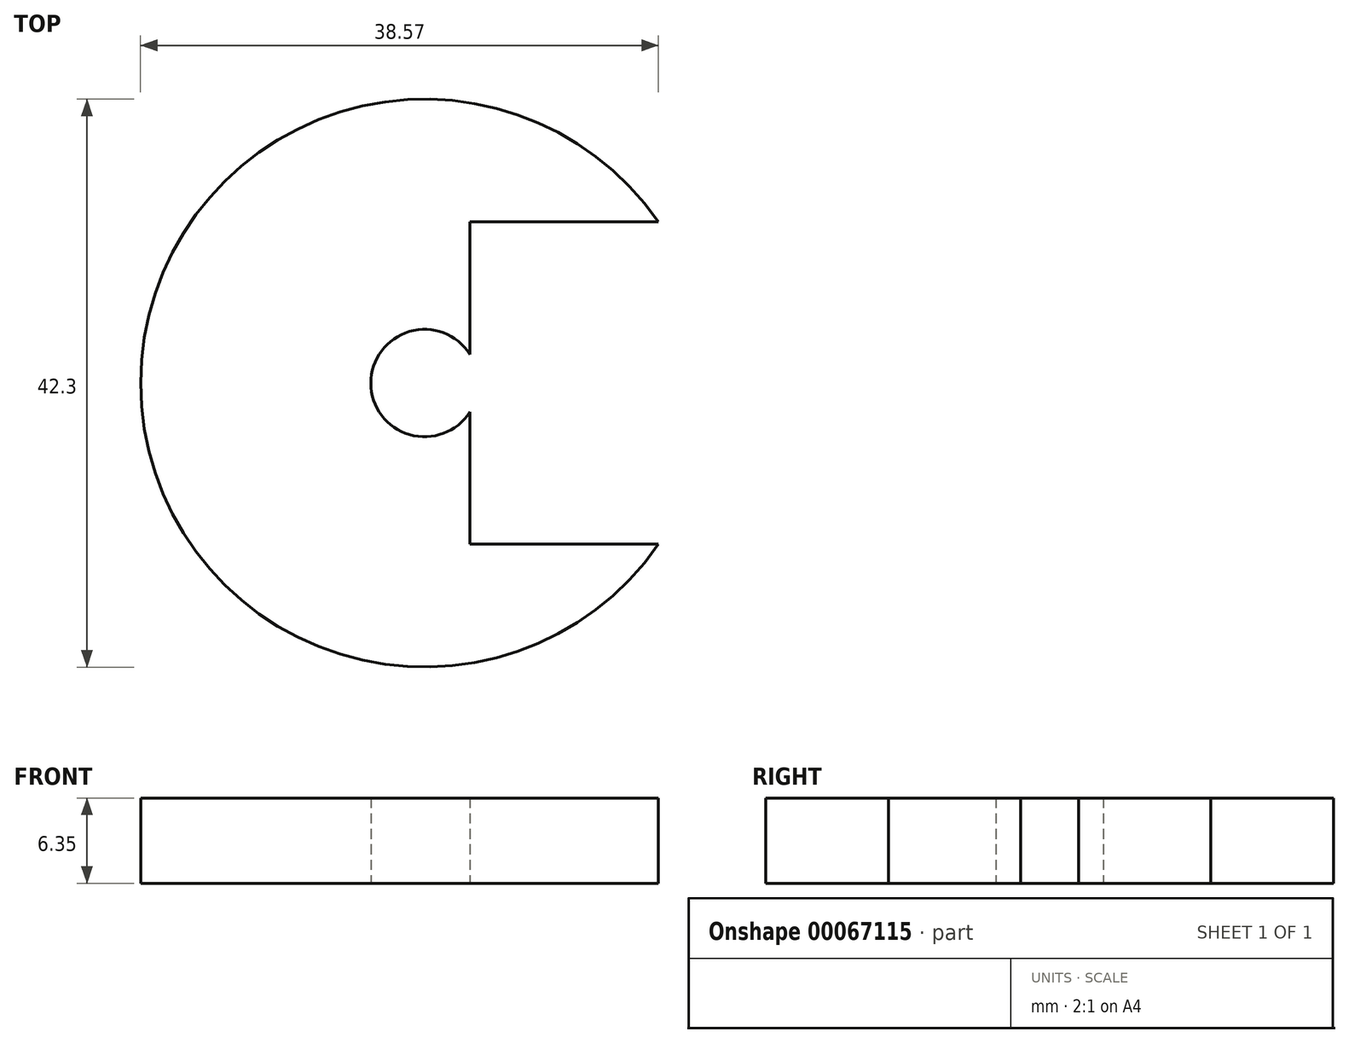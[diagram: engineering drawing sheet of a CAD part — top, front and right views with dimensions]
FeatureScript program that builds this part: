
annotation { "Feature Type Name" : "Feature", "Feature Type Description" : "" }
export const myFeature = defineFeature(function(context is Context, id is Id, definition is map)
    precondition{}
    {
        {
            var Q0;
            Q0=qCreatedBy(makeId("Top.planeOp"),FACE);
            var sketch = newSketch(context, id + "F0", { "sketchPlane" : qUnion([Q0])});
            skCircle(sketch, "E0", {"center": v(-6.29, 0) * mm, "radius": 21.15 * mm});
            skCircle(sketch, "E1", {"center": v(-6.29, 0) * mm, "radius": 4 * mm});
            skLineSegment(sketch, "E2.bottom", {"start": v(-2.92, 12) * mm, "end": v(14.86, 12) * mm});
            skLineSegment(sketch, "E2.top", {"start": v(-2.92, -12) * mm, "end": v(14.86, -12) * mm});
            skLineSegment(sketch, "E2.left", {"start": v(-2.92, 12) * mm, "end": v(-2.92, -12) * mm});
            skLineSegment(sketch, "E2.right", {"start": v(14.86, 12) * mm, "end": v(14.86, -12) * mm});
            skLineSegment(sketch, "E3", {"start": v(-6.29, 21.15) * mm, "end": v(-6.29, 24.32) * mm, "construction": true});
            skLineSegment(sketch, "E4", {"start": v(-6.29, -21.15) * mm, "end": v(-6.29, -24.33) * mm, "construction": true});
            skSolve(sketch);
        }
        {
            var Q0;
            {var subQ3=sQuery(id+"F0.wireOp",EDGE,"E0");var subQ5=sQuery(id+"F0.wireOp",EDGE,"E2.bottom");var subQ7=makeQuery(id+"F0.imprint","INTERSECT",VERTEX,{"derivedFrom":[subQ3,subQ5]});Q0=makeQuery(id+"F0.imprint","IMPRINT",FACE,{"disambiguationData":[TD([[makeQuery(id+"F0.imprint","IMPRINT",EDGE,{"disambiguationData":[TD([[subQ7,-1.0]])],"derivedFrom":subQ3}),1.0]])]});}
            extrude(context, id + "F1", {"entities" : qUnion([Q0]), "depth" : 6.35 * mm});
        }
    });
